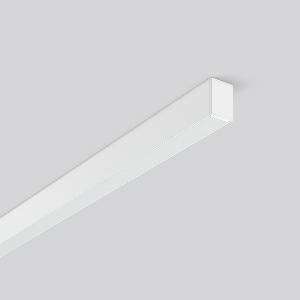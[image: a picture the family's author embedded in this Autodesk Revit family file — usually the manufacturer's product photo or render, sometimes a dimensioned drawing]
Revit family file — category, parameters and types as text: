
# Revit family: less_is_more_27_312196_002_76_e961
name_source: partatom
category: Lighting Fixtures
units: mm (PartAtom-declared; Revit-internal decimal feet)

## family parameters
Cut with Voids When Loaded = No
Host = Face
Light Source = No
Part Type = Normal
Room Calculation Point = No
Round Connector Dimension = Use Diameter
Shared = No

## types (1)
- LESS IS MORE 27 (1 x LED Modul 830, 1950 lm, 3000)
    Apparent Load = 29 VA
    CIE Flux Codes = 48 79 96 100 100
    Color Rendering = 80
    Color Temperature = 3000
    Default Elevation = 1800 mm
    Description = Series: LESS IS MORE 27
Ceiling and wall luminaire with slim design. Housing: extruded aluminium profile, powder-coated. End cap aluminium powder-coated. Diffuser made of non-yellowing plastic (PMMA), opal. Suitable for Ceiling mounting, Wall (surface). External driver with connecting cable. 
Colour: traffic white, matt (RAL 9016)
Length: 1012 mm
Width: 28 mm
Height: 38 mm
Lamp: LED
Socket: without socket
Colour temperature: 3000K
Colour rendering index (CRI): 82
System power: 29 W
Rated luminous flux: 1950 lm
Luminous efficiency: 67 lm/W
Control gear: Voltage converter, DALI dim.
Protection class: II
Type of protection: IP 20
    Height = 38 mm
    Lamp = 1 x LED Modul 830
    Lamp Light Flux = 1950 lm
    Lamp count = 1
    Length = 1012 mm
    Lifetime = 50000 h
    Luminous efficacy = 67 lm/W
    Manufacturer = RZB
    ModVariant = No
    Model = 312196.002.76
    Mounting Place = Ceiling, Wall
    Mounting Type = Surface mounted
    Number of Poles = 1
    OnlyDefault = Yes
    Power Factor = 1
    Product Name = LESS IS MORE 27
    Product group = Surface mounted LED linear luminaires
    ProductGroupID = 307
    Protection Class = Protection class II
    Protection Degree = IP 20
    RLX_Detail_Level = 1
    RLX_Emergency_Light_Flux = 0 lm
    RLX_Emergency_Type = 0
    RLX_Emergency_Type_DB = No
    RlxData = <blob elided: 22745 chars, md5=d1a5df91>
    Socket = socket
    Standby Power = 0 W
    System Light Flux = 1950 lm
    System Power = 29 W
    Type Comments = Product without accessories
    Type Image = 312196.002.jpg
    URL = http://relux.com
    VarID = ---
    Voltage = 230 V
    Voltage Range = 220-240 V
    Weight = 0.00 kg
    Width = 28 mm

## geometry (parser evidence)
native form markers: Blend x4, Sweep x11
no freeform markers — native parametric forms only
